# Revit family: Versailles 400 Phase Dimmable
name_source: partatom
category: Lighting Fixtures
units: mm (PartAtom-declared; Revit-internal decimal feet)

## family parameters
Always vertical = Yes
Cut with Voids When Loaded = No
Host = Wall
Light Source = Yes
OmniClass Number = 23.80.70.00
OmniClass Title = Lighting
Part Type = Normal
Room Calculation Point = No
Round Connector Dimension = Use Diameter
Shared = No

## types (3) — shared parameters
Color Filter = 16777215
Colour Temperature = 3000 K
Dimmable = yes
Dimming Lamp Color Temperature Shift = <None>
Dimming Method = Phase Dimmable
Driver Included = Yes
Driver Required = No
Efficacy (lm/w) = 93
Electrical Class = 2
Emit from Line Length = 610 mm
Lamp = LED
Light Source Fixed = Yes
Location rating = IP44
Luminous Flux = 658 lm
Main Material = Metal - Steel
Manufacturer = Astro Lighting Ltd
Model = Versailles 250
Photometric Web File = 1380029_Versailles 400 Phase Dimmable_Photometry_IES_Iss.01.ies
Power (Watts) = 7.1
Product Location = Bathroom/Indoor
Tilt Angle = 0.00°
URL = www.astrolighting.com
zero-valued in all types: Default Elevation

## per-type parameters (varying)
| type | Main Finish | Product Name | Product SKU |
| Astro Versaiiles 400 Polished Chrome Phase Dimmable 1380029 | Polished Chrome | Versailles 400 Chrome Phase Dimmable | 1380029 |
| Astro Versailles 400 Bronze  Phase Dimmable 1380030 | Bronze | Versailles 400 Bronze  Phase Dimmable | 1380030 |
| Astro Versailles 400 Matt Gold Phase Dimmable 1380031 | Matt Gold | Versailles 400 Gold | 1380031 |

## geometry (parser evidence)
native form markers: Sweep x3
no freeform markers — native parametric forms only
